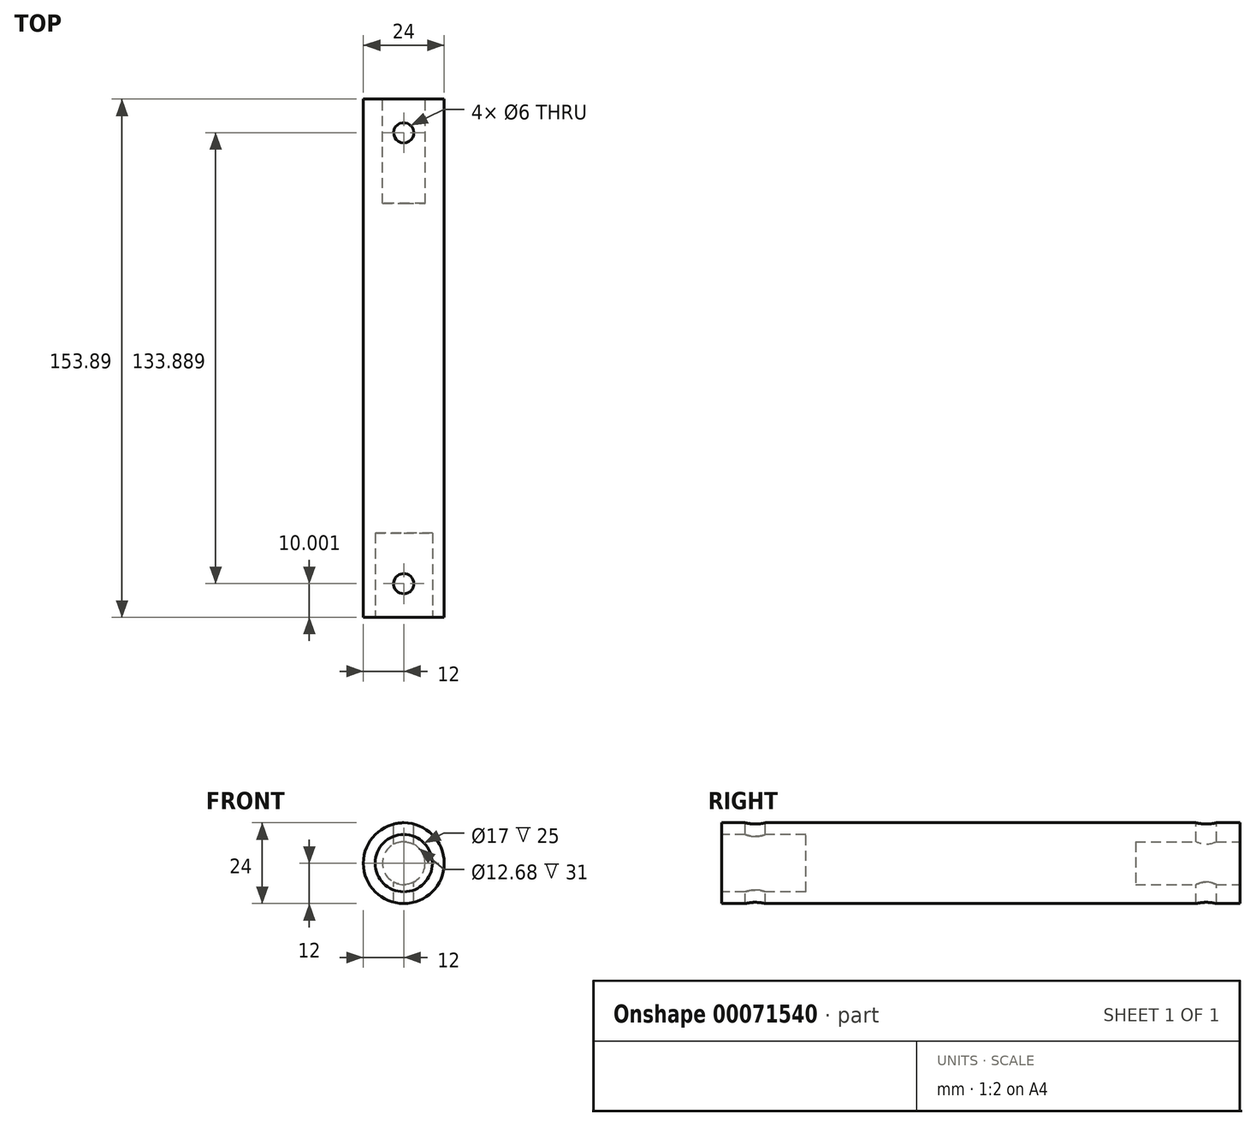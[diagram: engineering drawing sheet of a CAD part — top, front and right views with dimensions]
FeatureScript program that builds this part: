
annotation { "Feature Type Name" : "Feature", "Feature Type Description" : "" }
export const myFeature = defineFeature(function(context is Context, id is Id, definition is map)
    precondition{}
    {
        {
            var Q0;
            Q0=qCreatedBy(makeId("Front.planeOp"),FACE);
            var sketch = newSketch(context, id + "F0", { "sketchPlane" : qUnion([Q0])});
            skCircle(sketch, "E0", {"center": v(0, 0) * mm, "radius": 12 * mm});
            skSolve(sketch);
        }
        {
            var Q0;
            Q0 = qSketchRegion(id + "F0", true);
            extrude(context, id + "F1", {"entities" : qUnion([Q0]), "depth" : 153.89 * mm});
        }
        {
            var Q0;
            Q0=makeQuery(id+"F1.opExtrude","CAP_FACE",FACE,{"disambiguationData":[OSD([sQuery(id+"F0.wireOp",EDGE,"E0")])],"isStart":false});
            var sketch = newSketch(context, id + "F2", { "sketchPlane" : qUnion([Q0])});
            skCircle(sketch, "E1", {"center": v(0, 0) * mm, "radius": 8.5 * mm});
            skSolve(sketch);
        }
        {
            var Q0;
            Q0 = qSketchRegion(id + "F2", true);
            extrude(context, id + "F3", {"entities" : qUnion([Q0]), "operationType" : NewBodyOperationType.REMOVE, "oppositeDirection" : true, "depth" : 25 * mm});
        }
        {
            var Q0;
            Q0=makeQuery(id+"F1.opExtrude","CAP_FACE",FACE,{"disambiguationData":[OSD([sQuery(id+"F0.wireOp",EDGE,"E0")])],"isStart":true});
            var sketch = newSketch(context, id + "F4", { "sketchPlane" : qUnion([Q0])});
            skCircle(sketch, "E2", {"center": v(0, 0) * mm, "radius": 6.34 * mm});
            skSolve(sketch);
        }
        {
            var Q0;
            Q0 = qSketchRegion(id + "F4", true);
            extrude(context, id + "F5", {"entities" : qUnion([Q0]), "operationType" : NewBodyOperationType.REMOVE, "oppositeDirection" : true, "depth" : 31 * mm});
        }
        {
            var Q0;
            Q0=qCreatedBy(makeId("Top.planeOp"),FACE);
            var sketch = newSketch(context, id + "F6", { "sketchPlane" : qUnion([Q0])});
            skCircle(sketch, "E3", {"center": v(0, -10) * mm, "radius": 3 * mm});
            skCircle(sketch, "E4", {"center": v(0, -143.89) * mm, "radius": 3 * mm});
            skSolve(sketch);
        }
        {
            var Q0;
            Q0 = qSketchRegion(id + "F6", true);
            extrude(context, id + "F7", {"entities" : qUnion([Q0]), "operationType" : NewBodyOperationType.REMOVE, "oppositeDirection" : true, "depth" : 25 * mm, "hasSecondDirection" : true, "secondDirectionOppositeDirection" : false, "secondDirectionDepth" : 25 * mm});
        }
    });
